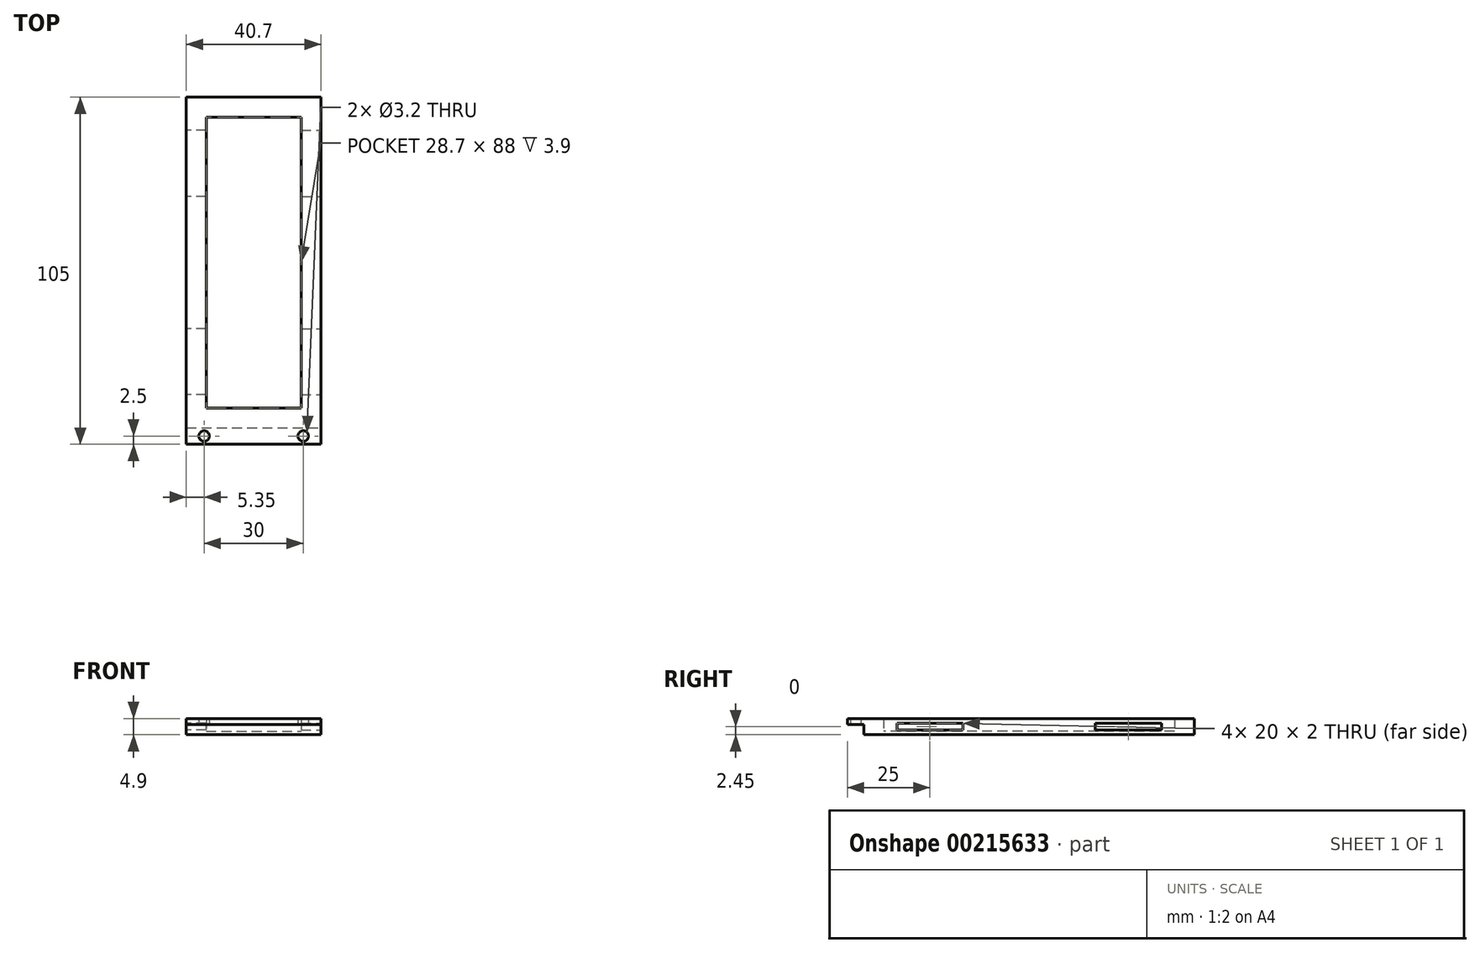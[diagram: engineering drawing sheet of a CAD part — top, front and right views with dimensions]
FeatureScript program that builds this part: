
annotation { "Feature Type Name" : "Feature", "Feature Type Description" : "" }
export const myFeature = defineFeature(function(context is Context, id is Id, definition is map)
    precondition{}
    {
        {
            var Q0;
            Q0=qCreatedBy(makeId("Top.planeOp"),FACE);
            var sketch = newSketch(context, id + "F0", { "sketchPlane" : qUnion([Q0])});
            skLineSegment(sketch, "E0.bottom", {"start": v(20.35, -50) * mm, "end": v(-20.35, -50) * mm});
            skLineSegment(sketch, "E0.top", {"start": v(20.35, 50) * mm, "end": v(-20.35, 50) * mm});
            skLineSegment(sketch, "E0.left", {"start": v(20.35, -50) * mm, "end": v(20.35, 50) * mm});
            skLineSegment(sketch, "E0.right", {"start": v(-20.35, -50) * mm, "end": v(-20.35, 50) * mm});
            skPoint(sketch, "E0.middle", {"position": v(0, 0) * mm});
            skSolve(sketch);
        }
        {
            var Q0;
            Q0 = qSketchRegion(id + "F0", true);
            extrude(context, id + "F1", {"entities" : qUnion([Q0]), "oppositeDirection" : true, "depth" : 1 * mm});
        }
        {
            var Q0;
            Q0=qCreatedBy(makeId("Top.planeOp"),FACE);
            var sketch = newSketch(context, id + "F2", { "sketchPlane" : qUnion([Q0])});
            skLineSegment(sketch, "E1.0", {"start": v(20.35, -50) * mm, "end": v(20.35, 50) * mm});
            skLineSegment(sketch, "E1.1", {"start": v(20.35, -50) * mm, "end": v(-20.35, -50) * mm});
            skLineSegment(sketch, "E1.2", {"start": v(-20.35, -50) * mm, "end": v(-20.35, 50) * mm});
            skLineSegment(sketch, "E1.3", {"start": v(20.35, 50) * mm, "end": v(-20.35, 50) * mm});
            skLineSegment(sketch, "E2.bottom", {"start": v(-20.35, 55) * mm, "end": v(20.35, 55) * mm});
            skLineSegment(sketch, "E2.top", {"start": v(-20.35, -55) * mm, "end": v(20.35, -55) * mm});
            skLineSegment(sketch, "E2.left", {"start": v(-20.35, 55) * mm, "end": v(-20.35, -55) * mm});
            skLineSegment(sketch, "E2.right", {"start": v(20.35, 55) * mm, "end": v(20.35, -55) * mm});
            skLineSegment(sketch, "E3.bottom", {"start": v(-14.35, 44) * mm, "end": v(14.35, 44) * mm});
            skLineSegment(sketch, "E3.top", {"start": v(-14.35, -44) * mm, "end": v(14.35, -44) * mm});
            skLineSegment(sketch, "E3.left", {"start": v(-14.35, 44) * mm, "end": v(-14.35, -44) * mm});
            skLineSegment(sketch, "E3.right", {"start": v(14.35, 44) * mm, "end": v(14.35, -44) * mm});
            skLineSegment(sketch, "E4", {"start": v(-20.35, 43.49) * mm, "end": v(-14.35, 43.49) * mm, "construction": true});
            skLineSegment(sketch, "E5", {"start": v(14.35, 17.35) * mm, "end": v(20.35, 17.35) * mm, "construction": true});
            skLineSegment(sketch, "E6", {"start": v(-11.01, 50) * mm, "end": v(-11.01, 44) * mm, "construction": true});
            skLineSegment(sketch, "E7", {"start": v(-13.27, -44) * mm, "end": v(-13.27, -50) * mm, "construction": true});
            skLineSegment(sketch, "E8.bottom", {"start": v(-3, 44) * mm, "end": v(3, 44) * mm});
            skLineSegment(sketch, "E8.top", {"start": v(-3, -44) * mm, "end": v(3, -44) * mm});
            skLineSegment(sketch, "E8.left", {"start": v(-3, 44) * mm, "end": v(-3, -44) * mm});
            skLineSegment(sketch, "E8.right", {"start": v(3, 44) * mm, "end": v(3, -44) * mm});
            skSolve(sketch);
        }
        {
            var Q0;
            {var subQ1=sQuery(id+"F2.wireOp",EDGE,"E1.1");Q0=makeQuery(id+"F2.imprint","IMPRINT",FACE,{"disambiguationData":[TD([[makeQuery(id+"F2.imprint","IMPRINT",EDGE,{"derivedFrom":subQ1}),-1.0]])]});}
            var Q1;
            Q1=makeQuery(id+"F2.imprint","IMPRINT",FACE,{"disambiguationData":[TD([[makeQuery(id+"F2.imprint","IMPRINT",EDGE,{"derivedFrom":sQuery(id+"F2.wireOp",EDGE,"E8.bottom")}),-1.0]])]});
            extrude(context, id + "F3", {"entities" : qUnion([Q0, Q1]), "operationType" : NewBodyOperationType.ADD, "depth" : 3.9 * mm});
        }
        {
            var Q0;
            Q0=makeQuery(id+"F3.boolean.opBoolean","MERGE",FACE,{"derivedFrom":[makeQuery(id+"F1.opExtrude","SWEPT_FACE",FACE,{"disambiguationData":[OSD([sQuery(id+"F0.wireOp",EDGE,"E0.bottom")])]}),makeQuery(id+"F3.opExtrude","SWEPT_FACE",FACE,{"disambiguationData":[OSD([sQuery(id+"F2.wireOp",EDGE,"E1.1")])]})]});
            var sketch = newSketch(context, id + "F4", { "sketchPlane" : qUnion([Q0])});
            skLineSegment(sketch, "E9.bottom", {"start": v(-20.35, 3.9) * mm, "end": v(20.35, 3.9) * mm});
            skLineSegment(sketch, "E9.top", {"start": v(-20.35, 2.05) * mm, "end": v(20.35, 2.05) * mm});
            skLineSegment(sketch, "E9.left", {"start": v(-20.35, 3.9) * mm, "end": v(-20.35, 2.05) * mm});
            skLineSegment(sketch, "E9.right", {"start": v(20.35, 3.9) * mm, "end": v(20.35, 2.05) * mm});
            skSolve(sketch);
        }
        {
            var Q0;
            Q0 = qSketchRegion(id + "F4", true);
            extrude(context, id + "F5", {"entities" : qUnion([Q0]), "operationType" : NewBodyOperationType.ADD, "depth" : 5 * mm});
        }
        {
            var Q0;
            Q0=makeQuery(id+"F5.opExtrude","SWEPT_FACE",FACE,{"disambiguationData":[OSD([sQuery(id+"F4.wireOp",EDGE,"E9.top")])]});
            var sketch = newSketch(context, id + "F6", { "sketchPlane" : qUnion([Q0])});
            skCircle(sketch, "E10", {"center": v(-15, 52.5) * mm, "radius": 1.6 * mm});
            skPoint(sketch, "E10.centerSnap0", {"position": v(-20.35, 52.5) * mm});
            skCircle(sketch, "E11", {"center": v(15, 52.5) * mm, "radius": 1.6 * mm});
            skPoint(sketch, "E11.centerSnap0", {"position": v(20.35, 52.5) * mm});
            skCircle(sketch, "E12.MirrorC", {"center": v(-15, -52.5) * mm, "radius": 1.6 * mm});
            skCircle(sketch, "E13.MirrorC", {"center": v(15, -52.5) * mm, "radius": 1.6 * mm});
            skSolve(sketch);
        }
        {
            var Q0;
            Q0 = qSketchRegion(id + "F6", true);
            extrude(context, id + "F7", {"entities" : qUnion([Q0]), "operationType" : NewBodyOperationType.REMOVE, "endBound" : BoundingType.THROUGH_ALL, "oppositeDirection" : true, "depth" : 25 * mm});
        }
        {
            var Q0;
            {var subQ0=sQuery(id+"F4.wireOp",EDGE,"E9.left");Q0=makeQuery(id+"Fv5G8qKNFdckqWy_1.1.F5.boolean.opBoolean","MERGE",FACE,{"derivedFrom":[makeQuery(id+"F5.boolean.opBoolean","MERGE",FACE,{"derivedFrom":[makeQuery(id+"F3.boolean.opBoolean","MERGE",FACE,{"derivedFrom":[makeQuery(id+"F1.opExtrude","SWEPT_FACE",FACE,{"disambiguationData":[OSD([sQuery(id+"F0.wireOp",EDGE,"E0.right")])]}),makeQuery(id+"F3.opExtrude","SWEPT_FACE",FACE,{"disambiguationData":[OSD([sQuery(id+"F2.wireOp",EDGE,"E2.left")])]})]}),makeQuery(id+"F5.opExtrude","SWEPT_FACE",FACE,{"disambiguationData":[OSD([subQ0])]})]}),makeQuery(id+"Fv5G8qKNFdckqWy_1.1.F5.opExtrude","SWEPT_FACE",FACE,{"disambiguationData":[OSD([subQ0])]})]});}
            var sketch = newSketch(context, id + "F8", { "sketchPlane" : qUnion([Q0])});
            skLineSegment(sketch, "E14", {"start": v(-48, 3.9) * mm, "end": v(-48, -1) * mm, "construction": true});
            skLineSegment(sketch, "E15.bottom", {"start": v(-20, 0.45) * mm, "end": v(-40, 0.45) * mm});
            skLineSegment(sketch, "E15.top", {"start": v(-20, 2.45) * mm, "end": v(-40, 2.45) * mm});
            skLineSegment(sketch, "E15.left", {"start": v(-20, 0.45) * mm, "end": v(-20, 2.45) * mm});
            skLineSegment(sketch, "E15.right", {"start": v(-40, 0.45) * mm, "end": v(-40, 2.45) * mm});
            skPoint(sketch, "E15.middle", {"position": v(-30, 1.45) * mm});
            skPoint(sketch, "E15.middle.positionSnap0", {"position": v(-48, 1.45) * mm});
            skPoint(sketch, "E15.centerSnap0", {"position": v(-48, 1.45) * mm});
            skLineSegment(sketch, "E16.bottom", {"start": v(20, 0.45) * mm, "end": v(40, 0.45) * mm});
            skLineSegment(sketch, "E16.top", {"start": v(20, 2.45) * mm, "end": v(40, 2.45) * mm});
            skLineSegment(sketch, "E16.left", {"start": v(20, 0.45) * mm, "end": v(20, 2.45) * mm});
            skLineSegment(sketch, "E16.right", {"start": v(40, 0.45) * mm, "end": v(40, 2.45) * mm});
            skPoint(sketch, "E16.middle", {"position": v(30, 1.45) * mm});
            skSolve(sketch);
        }
        {
            var Q0;
            Q0 = qSketchRegion(id + "F8", true);
            var Q1;
            Q1=makeQuery(id+"F3.opExtrude","SWEPT_FACE",FACE,{"disambiguationData":[OSD([sQuery(id+"F2.wireOp",EDGE,"E3.left")])]});
            extrude(context, id + "F9", {"entities" : qUnion([Q0]), "operationType" : NewBodyOperationType.REMOVE, "endBound" : BoundingType.UP_TO_SURFACE, "oppositeDirection" : true, "endBoundEntityFace" : qUnion([Q1]), "depth" : 25 * mm});
        }
        {
            var Q0;
            {var subQ0=sQuery(id+"F4.wireOp",EDGE,"E9.right");Q0=makeQuery(id+"Fv5G8qKNFdckqWy_1.1.F5.boolean.opBoolean","MERGE",FACE,{"derivedFrom":[makeQuery(id+"F5.boolean.opBoolean","MERGE",FACE,{"derivedFrom":[makeQuery(id+"F3.boolean.opBoolean","MERGE",FACE,{"derivedFrom":[makeQuery(id+"F1.opExtrude","SWEPT_FACE",FACE,{"disambiguationData":[OSD([sQuery(id+"F0.wireOp",EDGE,"E0.left")])]}),makeQuery(id+"F3.opExtrude","SWEPT_FACE",FACE,{"disambiguationData":[OSD([sQuery(id+"F2.wireOp",EDGE,"E2.right")])]})]}),makeQuery(id+"F5.opExtrude","SWEPT_FACE",FACE,{"disambiguationData":[OSD([subQ0])]})]}),makeQuery(id+"Fv5G8qKNFdckqWy_1.1.F5.opExtrude","SWEPT_FACE",FACE,{"disambiguationData":[OSD([subQ0])]})]});}
            var sketch = newSketch(context, id + "F10", { "sketchPlane" : qUnion([Q0])});
            skLineSegment(sketch, "E17.0", {"start": v(-20, 2.45) * mm, "end": v(-40, 2.45) * mm});
            skLineSegment(sketch, "E18.0", {"start": v(-20, 0.45) * mm, "end": v(-20, 2.45) * mm});
            skLineSegment(sketch, "E19.0", {"start": v(-20, 0.45) * mm, "end": v(-40, 0.45) * mm});
            skLineSegment(sketch, "E20.0", {"start": v(-40, 0.45) * mm, "end": v(-40, 2.45) * mm});
            skLineSegment(sketch, "E21.0", {"start": v(20, 0.45) * mm, "end": v(20, 2.45) * mm});
            skLineSegment(sketch, "E22.0", {"start": v(20, 2.45) * mm, "end": v(40, 2.45) * mm});
            skLineSegment(sketch, "E23.0", {"start": v(40, 0.45) * mm, "end": v(40, 2.45) * mm});
            skLineSegment(sketch, "E24.0", {"start": v(20, 0.45) * mm, "end": v(40, 0.45) * mm});
            skSolve(sketch);
        }
        {
            var Q0;
            Q0 = qSketchRegion(id + "F10", true);
            var Q1;
            Q1=makeQuery(id+"F3.opExtrude","SWEPT_FACE",FACE,{"disambiguationData":[OSD([sQuery(id+"F2.wireOp",EDGE,"E3.right")])]});
            extrude(context, id + "F11", {"entities" : qUnion([Q0]), "operationType" : NewBodyOperationType.REMOVE, "endBound" : BoundingType.UP_TO_SURFACE, "oppositeDirection" : true, "endBoundEntityFace" : qUnion([Q1]), "depth" : 25 * mm});
        }
    });
